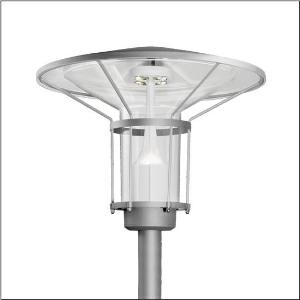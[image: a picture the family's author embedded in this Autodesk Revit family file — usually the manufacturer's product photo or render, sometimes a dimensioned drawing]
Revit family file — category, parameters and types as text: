
# Revit family: laterne_classic_iq___p1_0a_5xa5245bf14h_da05
name_source: partatom
category: Lighting Fixtures
units: mm (PartAtom-declared; Revit-internal decimal feet)

## family parameters
Cut with Voids When Loaded = No
Host = Face
Light Source = No
Part Type = Normal
Room Calculation Point = No
Round Connector Dimension = Use Diameter
Shared = No

## types (1)
- --- (1 x LED, 1360 lm, 12.9 W, 2200K)
    Apparent Load = 13 VA
    CIE Flux Codes = 30 61 91 96 100
    Color Rendering = 70
    Color Temperature = 2200K
    Default Elevation = 1800 mm
    Description = Lantern Classic iQ, mast luminaire, Module 540 iQ-SR, primary light control with 3 zone facetted reflector, of plastic, silver coated, highly specular, structured, primary optical cover: cover, of PMMA, transparent, light distribution: P1.0a, light emission: direct distribution, primary light characteristic: strongly asymmetric, installation type: post-top, LED, High Power LED, rated luminous flux: 1.360lm, luminous efficacy: 105lm/W, light colour: 722, colour temperature: 2200K, control gear: ECG iQ, control: presetting dimming logarithmic, Street-Remote, Auto-Match, Temp-Guard, Lumen-Switch, Night-Set, Smart-Wire, Light-Fading, Desk-Remote (wireless, voltage-free reading and setting of iQ features in the workshop via application-optimized NFC function/RFID function), optimised constant luminous flux control (CLO 2.0), with terminal, 6-pole, max. 2.5mm², mains connection: 230..240V, AC, 50/60Hz, start of lifetime: 13W, end of service life: 13W, reduction: 6W, luminaire housing, upper part, of glass-fibre reinforced polyester, coated, Siteco® metallic grey (DB 702S), diameter: 750mm, height: 596mm, spigot size: d x l = 76 x 70mm (post-top) | with reducer (optional accessory) 60 x 70mm, post-top mast mounting element, of diecast aluminium, coated, Siteco® metallic grey (DB 702S), Module 540 iQ-SR, traffic white (RAL 9016), equipment: standard, protection rating (complete): IP65, insulation class (complete): insulation class II (safety insulation), certification: CE, ENEC, VDE, packaging unit: 1 piece

Light Distribution: P1.0a
    Height = 596 mm
    Lamp = 1 x LED
    Lamp Light Flux = 1360 lm
    Lamp Power = 12.9 W
    Lamp count = 1
    Length = 750 mm
    Luminous efficacy = 105 lm/W
    Manufacturer = Siteco
    ModVariant = No
    Model = 5XA5245BF14H
    Number of Poles = 1
    OnlyDefault = Yes
    Power Factor = 1
    Product Name = Laterne Classic iQ | P1.0a
    Product group = mast luminaire | pylon top
    ProductGroupID = 6100
    Protection Class = Protection class II
    Protection Degree = IP 65
    RLX_Detail_Level = 1
    RLX_Emergency_Light_Flux = 0 lm
    RLX_Emergency_Type = 0
    RLX_Emergency_Type_DB = No
    RlxData = <blob elided: 94293 chars, md5=c6cccd5b>
    Socket = socket
    Standby Power = 0 W
    System Light Flux = 1360 lm
    System Power = 13 W
    Type Comments = factory setting: luminous flux: 100 % | dim-lin: 254 | 516 mA
    Type Image = l_1006052.jpg
    URL = http://relux.com
    VarID = @adj_092601
    Voltage = 0 V
    Weight = 0.00 kg
    Width = 0 mm  [stored 0 ft]

note: [stored X ft] marks values corroborated as IEEE doubles in the binary element streams (Revit-internal decimal feet)

## geometry (parser evidence)
native form markers: Blend x4, Sweep x9
no freeform markers — native parametric forms only
